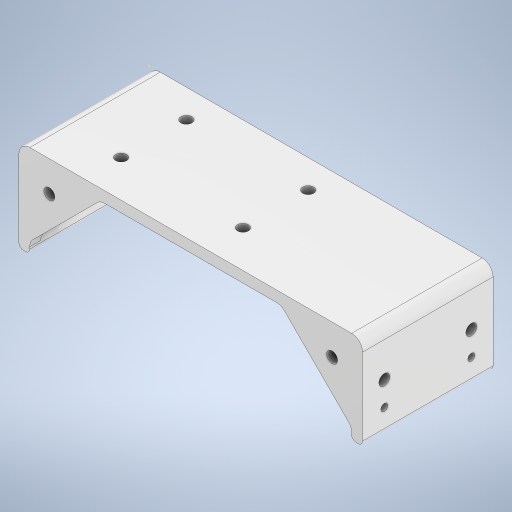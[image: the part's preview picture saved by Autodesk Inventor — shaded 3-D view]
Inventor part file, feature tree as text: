
AUTODESK INVENTOR PART (.ipt)
format: ipt  version: 2024.3 (Build 283343000, 343)  size: 468,992 bytes
history: native  units: mm
features: sketch x12, extrude x8, fillet x3, hole x2, projected_geometry x2, other x1
ambient origin geometry x8: Origin, YZ Plane, XZ Plane, XY Plane, X Axis, Y Axis, Z Axis, Center Point
bodies: Body1 (feature_tree)
feature tree (28):
  other  "ソリッド1"
  extrude  "押し出し1"  Depth=158.0mm
  extrude  "押し出し3"  Depth=250.0mm
  extrude  "押し出し4"  Depth=5.0mm
  hole  "穴2"  [1 undecoded]
  extrude  "押し出し5"  Depth=50.0mm
  extrude  "押し出し6"  Depth=50.0mm
  extrude  "押し出し7"  Depth=30.0mm
  fillet  "フィレット4"  Radius=5.0mm
  fillet  "フィレット6"  Radius=50.0mm
  extrude  "押し出し8"  Depth=50.0mm
  fillet  "フィレット7"  Radius=30.0mm
  sketch  "スケッチ13"
  sketch  "スケッチ14"
  hole  "穴3"  [1 undecoded]
  extrude  "押し出し9"  Depth=5.0mm TaperAngle=0.0deg
  sketch  "スケッチ1"
  sketch  "スケッチ5"
  sketch  "スケッチ6"
  sketch  "スケッチ7"
  sketch  "スケッチ8"
  sketch  "スケッチ9"
  sketch  "スケッチ10"
  sketch  "スケッチ12"
  projected_geometry  "投影ループ1"
  sketch  "スケッチ15"
  sketch  "スケッチ16"
  projected_geometry  "投影ループ2"
note: 2 required parameter values undecoded (feature->parameter linkage not recoverable at this tier; creation-order binding heuristic only, values carry confidence <= 0.55)
